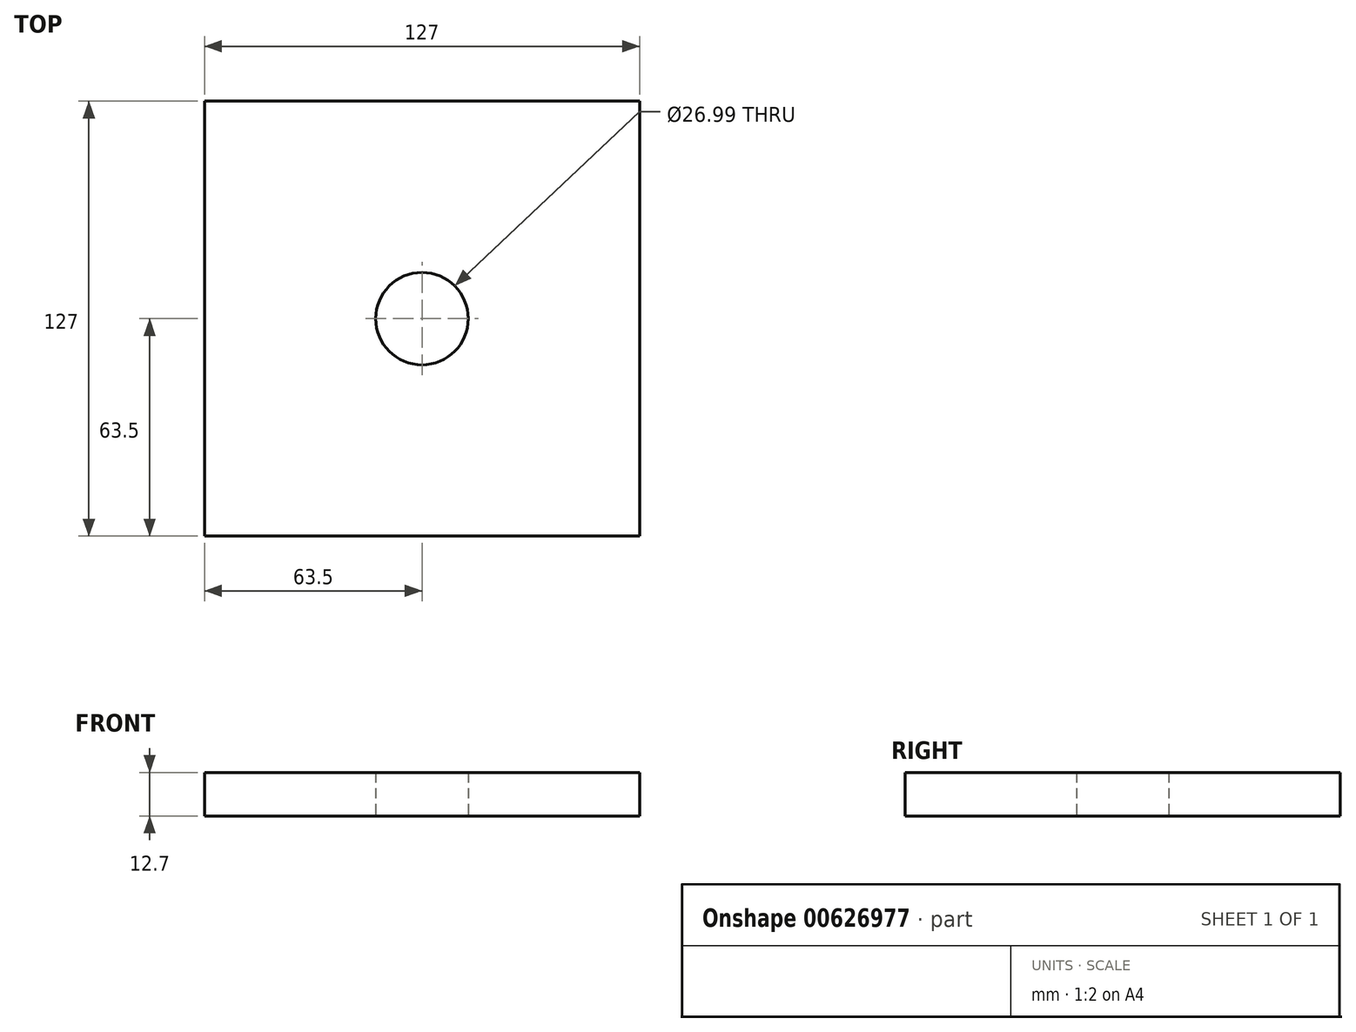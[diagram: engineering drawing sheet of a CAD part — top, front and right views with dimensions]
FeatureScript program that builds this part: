
annotation { "Feature Type Name" : "Feature", "Feature Type Description" : "" }
export const myFeature = defineFeature(function(context is Context, id is Id, definition is map)
    precondition{}
    {
        {
            var Q0;
            Q0=qCreatedBy(makeId("Top.planeOp"),FACE);
            var sketch = newSketch(context, id + "F0", { "sketchPlane" : qUnion([Q0])});
            skLineSegment(sketch, "E0.bottom", {"start": v(63.5, -63.5) * mm, "end": v(-63.5, -63.5) * mm});
            skLineSegment(sketch, "E0.top", {"start": v(63.5, 63.5) * mm, "end": v(-63.5, 63.5) * mm});
            skLineSegment(sketch, "E0.left", {"start": v(63.5, -63.5) * mm, "end": v(63.5, 63.5) * mm});
            skLineSegment(sketch, "E0.right", {"start": v(-63.5, -63.5) * mm, "end": v(-63.5, 63.5) * mm});
            skPoint(sketch, "E0.middle", {"position": v(0, 0) * mm});
            skCircle(sketch, "E1", {"center": v(0, 0) * mm, "radius": 13.5 * mm});
            skSolve(sketch);
        }
        {
            var Q0;
            Q0 = qSketchRegion(id + "F0", true);
            extrude(context, id + "F1", {"entities" : qUnion([Q0]), "depth" : 12.7 * mm, "offsetDistance" : 25.4 * mm});
        }
    });
